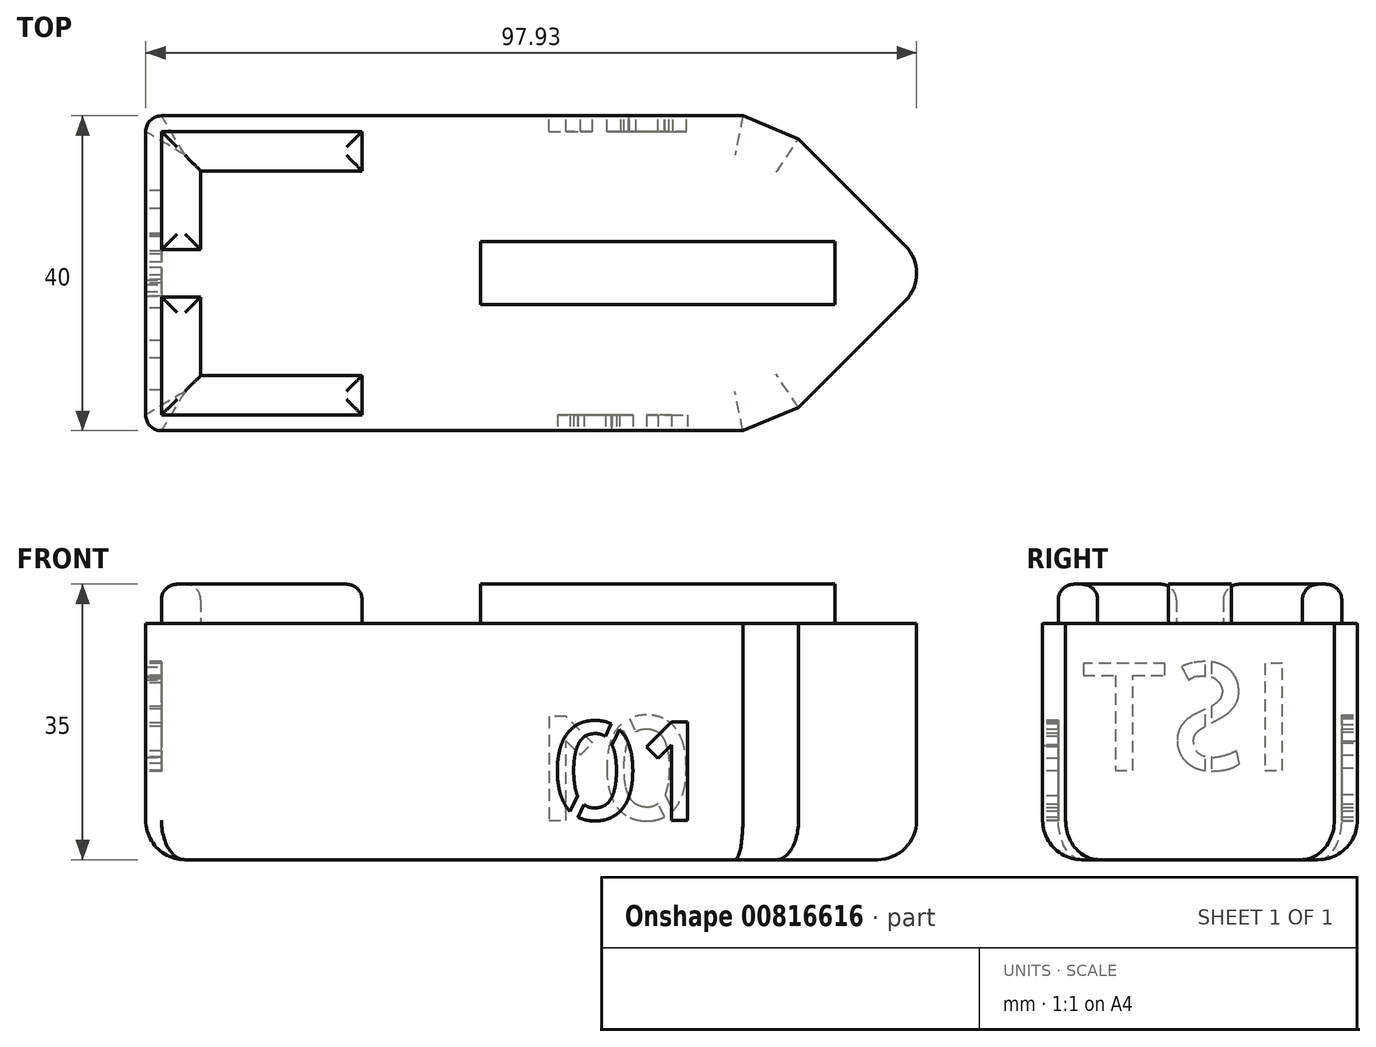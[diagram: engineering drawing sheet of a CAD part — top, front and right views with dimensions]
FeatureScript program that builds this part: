
annotation { "Feature Type Name" : "Feature", "Feature Type Description" : "" }
export const myFeature = defineFeature(function(context is Context, id is Id, definition is map)
    precondition{}
    {
        {
            var Q0;
            Q0=qCreatedBy(makeId("Top.planeOp"),FACE);
            var sketch = newSketch(context, id + "F0", { "sketchPlane" : qUnion([Q0])});
            skLineSegment(sketch, "E0.bottom", {"start": v(-50, 20) * mm, "end": v(50, 20) * mm});
            skLineSegment(sketch, "E0.top", {"start": v(-50, -20) * mm, "end": v(50, -20) * mm});
            skLineSegment(sketch, "E0.left", {"start": v(-50, 20) * mm, "end": v(-50, -20) * mm});
            skLineSegment(sketch, "E0.right", {"start": v(50, 20) * mm, "end": v(50, -20) * mm});
            skPoint(sketch, "E0.middle", {"position": v(0, 0) * mm});
            skSolve(sketch);
        }
        {
            var Q0;
            Q0 = qSketchRegion(id + "F0", true);
            extrude(context, id + "F1", {"entities" : qUnion([Q0]), "depth" : 30 * mm, "offsetDistance" : 25 * mm});
        }
        {
            var Q0;
            Q0=makeQuery(id+"F1.opExtrude","SWEPT_EDGE",EDGE,{"disambiguationData":[OSD([sQuery(id+"F0.wireOp",EDGE,"E0.top"),sQuery(id+"F0.wireOp",EDGE,"E0.right")])]});
            var Q1;
            Q1=makeQuery(id+"F1.opExtrude","SWEPT_EDGE",EDGE,{"disambiguationData":[OSD([sQuery(id+"F0.wireOp",EDGE,"E0.bottom"),sQuery(id+"F0.wireOp",EDGE,"E0.right")])]});
            chamfer(context, id + "F2", {"entities" : qUnion([Q0, Q1]), "width" : 20 * mm, "tangentPropagation" : true});
        }
        {
            var Q0;
            {var subQ0=sQuery(id+"F0.wireOp",EDGE,"E0.right");Q0=makeQuery(id+"F2.opChamfer","BLEND_EDGE",EDGE,{"blendedFrom":[makeQuery(id+"F1.opExtrude","SWEPT_EDGE",EDGE,{"disambiguationData":[OSD([sQuery(id+"F0.wireOp",EDGE,"E0.bottom"),subQ0])]}),makeQuery(id+"F1.opExtrude","SWEPT_EDGE",EDGE,{"disambiguationData":[OSD([sQuery(id+"F0.wireOp",EDGE,"E0.top"),subQ0])]})],"blendedInto":[]});}
            fillet(context, id + "F3", {"entities" : qUnion([Q0]), "radius" : 5 * mm, "tangentPropagation" : true, "allowEdgeOverflow" : false});
        }
        {
            var Q0;
            Q0=makeQuery(id+"F1.opExtrude","CAP_FACE",FACE,{"disambiguationData":[OSD([sQuery(id+"F0.wireOp",EDGE,"E0.bottom"),sQuery(id+"F0.wireOp",EDGE,"E0.top"),sQuery(id+"F0.wireOp",EDGE,"E0.left"),sQuery(id+"F0.wireOp",EDGE,"E0.right")])],"isStart":false});
            var sketch = newSketch(context, id + "F4", { "sketchPlane" : qUnion([Q0])});
            skPoint(sketch, "E1.middle", {"position": v(0, 0) * mm});
            skLineSegment(sketch, "E2", {"start": v(15.03, 0) * mm, "end": v(47.93, 0) * mm});
            skPoint(sketch, "E1.left.start.orphan", {"position": v(-22.5, 4) * mm});
            skPoint(sketch, "E1.top.start.orphan", {"position": v(-22.5, -4) * mm});
            skPoint(sketch, "E3.orphan", {"position": v(22.5, 4) * mm});
            skPoint(sketch, "E1.right.end.orphan", {"position": v(22.5, -4) * mm});
            skLineSegment(sketch, "E4.bottom", {"start": v(-7.47, 4) * mm, "end": v(37.53, 4) * mm});
            skLineSegment(sketch, "E4.top", {"start": v(-7.47, -4) * mm, "end": v(37.53, -4) * mm});
            skLineSegment(sketch, "E4.left", {"start": v(-7.47, 4) * mm, "end": v(-7.47, -4) * mm});
            skLineSegment(sketch, "E4.right", {"start": v(37.53, 4) * mm, "end": v(37.53, -4) * mm});
            skPoint(sketch, "E4.middle", {"position": v(15.03, 0) * mm});
            skSolve(sketch);
        }
        {
            var Q0;
            Q0=makeQuery(id+"F1.opExtrude","SWEPT_EDGE",EDGE,{"disambiguationData":[OSD([sQuery(id+"F0.wireOp",EDGE,"E0.top"),sQuery(id+"F0.wireOp",EDGE,"E0.left")])]});
            var Q1;
            Q1=makeQuery(id+"F1.opExtrude","SWEPT_EDGE",EDGE,{"disambiguationData":[OSD([sQuery(id+"F0.wireOp",EDGE,"E0.bottom"),sQuery(id+"F0.wireOp",EDGE,"E0.left")])]});
            fillet(context, id + "F5", {"entities" : qUnion([Q0, Q1]), "radius" : 2 * mm, "tangentPropagation" : true, "allowEdgeOverflow" : false});
        }
        {
            var Q0;
            Q0=makeQuery(id+"F1.opExtrude","CAP_FACE",FACE,{"disambiguationData":[OSD([sQuery(id+"F0.wireOp",EDGE,"E0.bottom"),sQuery(id+"F0.wireOp",EDGE,"E0.top"),sQuery(id+"F0.wireOp",EDGE,"E0.left"),sQuery(id+"F0.wireOp",EDGE,"E0.right")])],"isStart":false});
            var sketch = newSketch(context, id + "F6", { "sketchPlane" : qUnion([Q0])});
            skLineSegment(sketch, "E5.bottom", {"start": v(-48, 18) * mm, "end": v(-22.5, 18) * mm});
            skLineSegment(sketch, "E5.top", {"start": v(-48, 13) * mm, "end": v(-22.5, 13) * mm});
            skLineSegment(sketch, "E5.left", {"start": v(-48, 18) * mm, "end": v(-48, 13) * mm});
            skLineSegment(sketch, "E5.right", {"start": v(-22.5, 18) * mm, "end": v(-22.5, 13) * mm});
            skLineSegment(sketch, "E6.bottom", {"start": v(-48, -18) * mm, "end": v(-22.5, -18) * mm});
            skLineSegment(sketch, "E6.top", {"start": v(-48, -13) * mm, "end": v(-22.5, -13) * mm});
            skLineSegment(sketch, "E6.left", {"start": v(-48, -18) * mm, "end": v(-48, -13) * mm});
            skLineSegment(sketch, "E6.right", {"start": v(-22.5, -18) * mm, "end": v(-22.5, -13) * mm});
            skSolve(sketch);
        }
        {
            var Q0;
            Q0=makeQuery(id+"F6.imprint","IMPRINT",FACE,{"disambiguationData":[TD([[makeQuery(id+"F6.imprint","IMPRINT",EDGE,{"derivedFrom":sQuery(id+"F6.wireOp",EDGE,"E5.bottom")}),-1.0]])]});
            var Q1;
            Q1=makeQuery(id+"F6.imprint","IMPRINT",FACE,{"disambiguationData":[TD([[makeQuery(id+"F6.imprint","IMPRINT",EDGE,{"derivedFrom":sQuery(id+"F6.wireOp",EDGE,"E6.bottom")}),1.0]])]});
            extrude(context, id + "F7", {"entities" : qUnion([Q0, Q1]), "operationType" : NewBodyOperationType.ADD, "depth" : 5 * mm, "offsetDistance" : 25 * mm});
        }
        {
            var Q0;
            Q0=makeQuery(id+"F1.opExtrude","CAP_FACE",FACE,{"disambiguationData":[OSD([sQuery(id+"F0.wireOp",EDGE,"E0.bottom"),sQuery(id+"F0.wireOp",EDGE,"E0.top"),sQuery(id+"F0.wireOp",EDGE,"E0.left"),sQuery(id+"F0.wireOp",EDGE,"E0.right")])],"isStart":false});
            var sketch = newSketch(context, id + "F8", { "sketchPlane" : qUnion([Q0])});
            skLineSegment(sketch, "E7.bottom", {"start": v(-48, 13) * mm, "end": v(-43, 13) * mm});
            skLineSegment(sketch, "E7.top", {"start": v(-48, 3) * mm, "end": v(-43, 3) * mm});
            skLineSegment(sketch, "E7.left", {"start": v(-48, 13) * mm, "end": v(-48, 3) * mm});
            skLineSegment(sketch, "E7.right", {"start": v(-43, 13) * mm, "end": v(-43, 3) * mm});
            skLineSegment(sketch, "E8.bottom", {"start": v(-48, -13) * mm, "end": v(-43, -13) * mm});
            skLineSegment(sketch, "E8.top", {"start": v(-48, -3) * mm, "end": v(-43, -3) * mm});
            skLineSegment(sketch, "E8.left", {"start": v(-48, -13) * mm, "end": v(-48, -3) * mm});
            skLineSegment(sketch, "E8.right", {"start": v(-43, -13) * mm, "end": v(-43, -3) * mm});
            skSolve(sketch);
        }
        {
            var Q0;
            Q0=makeQuery(id+"F8.imprint","IMPRINT",FACE,{"disambiguationData":[TD([[makeQuery(id+"F8.imprint","IMPRINT",EDGE,{"derivedFrom":sQuery(id+"F8.wireOp",EDGE,"E7.bottom")}),-1.0]])]});
            var Q1;
            Q1=makeQuery(id+"F8.imprint","IMPRINT",FACE,{"disambiguationData":[TD([[makeQuery(id+"F8.imprint","IMPRINT",EDGE,{"derivedFrom":sQuery(id+"F8.wireOp",EDGE,"E8.bottom")}),1.0]])]});
            extrude(context, id + "F9", {"entities" : qUnion([Q0, Q1]), "operationType" : NewBodyOperationType.ADD, "depth" : 5 * mm, "offsetDistance" : 25 * mm});
        }
        {
            var Q0;
            {var subQ0=sQuery(id+"F0.wireOp",EDGE,"E0.top");Q0=makeQuery(id+"F2.opChamfer","BLEND_EDGE",EDGE,{"blendedFrom":[makeQuery(id+"F1.opExtrude","SWEPT_EDGE",EDGE,{"disambiguationData":[OSD([subQ0,sQuery(id+"F0.wireOp",EDGE,"E0.right")])]}),makeQuery(id+"F1.opExtrude","SWEPT_FACE",FACE,{"disambiguationData":[OSD([subQ0])]})],"blendedInto":[makeQuery(id+"F1.opExtrude","SWEPT_FACE",FACE,{"disambiguationData":[OSD([subQ0])]})]});}
            var Q1;
            {var subQ0=sQuery(id+"F0.wireOp",EDGE,"E0.bottom");Q1=makeQuery(id+"F2.opChamfer","BLEND_EDGE",EDGE,{"blendedFrom":[makeQuery(id+"F1.opExtrude","SWEPT_EDGE",EDGE,{"disambiguationData":[OSD([subQ0,sQuery(id+"F0.wireOp",EDGE,"E0.right")])]}),makeQuery(id+"F1.opExtrude","SWEPT_FACE",FACE,{"disambiguationData":[OSD([subQ0])]})],"blendedInto":[makeQuery(id+"F1.opExtrude","SWEPT_FACE",FACE,{"disambiguationData":[OSD([subQ0])]})]});}
            chamfer(context, id + "F10", {"entities" : qUnion([Q0, Q1]), "width" : 10 * mm, "tangentPropagation" : true});
        }
        {
            var Q0;
            Q0=makeQuery(id+"F1.opExtrude","CAP_FACE",FACE,{"disambiguationData":[OSD([sQuery(id+"F0.wireOp",EDGE,"E0.bottom"),sQuery(id+"F0.wireOp",EDGE,"E0.top"),sQuery(id+"F0.wireOp",EDGE,"E0.left"),sQuery(id+"F0.wireOp",EDGE,"E0.right")])],"isStart":true});
            fillet(context, id + "F11", {"entities" : qUnion([Q0]), "radius" : 5 * mm, "tangentPropagation" : true, "allowEdgeOverflow" : false});
        }
        {
            var Q0;
            Q0=makeQuery(id+"F1.opExtrude","SWEPT_FACE",FACE,{"disambiguationData":[OSD([sQuery(id+"F0.wireOp",EDGE,"E0.top")])]});
            var sketch = newSketch(context, id + "F12", { "sketchPlane" : qUnion([Q0])});
            skText(sketch, "E9", { "text": "01\n", "fontName": "AllertaStencil-Regular.ttf"});
            const initialGuessF12  = {"E9": [0.00104, 0.005, 1, 0, 0.0125]};
            skSetInitialGuess(sketch, initialGuessF12);
            skSolve(sketch);
        }
        {
            var Q0;
            Q0 = qSketchRegion(id + "F12", true);
            extrude(context, id + "F13", {"entities" : qUnion([Q0]), "operationType" : NewBodyOperationType.REMOVE, "oppositeDirection" : true, "depth" : 2 * mm, "offsetDistance" : 25 * mm});
        }
        {
            var Q0;
            Q0=makeQuery(id+"F1.opExtrude","SWEPT_FACE",FACE,{"disambiguationData":[OSD([sQuery(id+"F0.wireOp",EDGE,"E0.bottom")])]});
            var sketch = newSketch(context, id + "F14", { "sketchPlane" : qUnion([Q0])});
            skText(sketch, "E10", { "text": "01", "fontName": "AllertaStencil-Regular.ttf"});
            const initialGuessF14  = {"E10": [-0.02, 0.005, 1, 0, 0.01318]};
            skSetInitialGuess(sketch, initialGuessF14);
            skSolve(sketch);
        }
        {
            var Q0;
            Q0 = qSketchRegion(id + "F14", true);
            extrude(context, id + "F15", {"entities" : qUnion([Q0]), "operationType" : NewBodyOperationType.REMOVE, "oppositeDirection" : true, "depth" : 2 * mm, "offsetDistance" : 25 * mm});
        }
        {
            var Q0;
            Q0=makeQuery(id+"F9.boolean.opBoolean","MERGE",FACE,{"derivedFrom":[makeQuery(id+"F7.opExtrude","CAP_FACE",FACE,{"disambiguationData":[OSD([sQuery(id+"F6.wireOp",EDGE,"E5.bottom"),sQuery(id+"F6.wireOp",EDGE,"E5.top"),sQuery(id+"F6.wireOp",EDGE,"E5.left"),sQuery(id+"F6.wireOp",EDGE,"E5.right")])],"isStart":false}),makeQuery(id+"F9.opExtrude","CAP_FACE",FACE,{"disambiguationData":[OSD([sQuery(id+"F8.wireOp",EDGE,"E7.bottom"),sQuery(id+"F8.wireOp",EDGE,"E7.top"),sQuery(id+"F8.wireOp",EDGE,"E7.left"),sQuery(id+"F8.wireOp",EDGE,"E7.right")])],"isStart":false})]});
            var Q1;
            Q1=makeQuery(id+"F9.boolean.opBoolean","MERGE",FACE,{"derivedFrom":[makeQuery(id+"F7.opExtrude","CAP_FACE",FACE,{"disambiguationData":[OSD([sQuery(id+"F6.wireOp",EDGE,"E6.bottom"),sQuery(id+"F6.wireOp",EDGE,"E6.top"),sQuery(id+"F6.wireOp",EDGE,"E6.left"),sQuery(id+"F6.wireOp",EDGE,"E6.right")])],"isStart":false}),makeQuery(id+"F9.opExtrude","CAP_FACE",FACE,{"disambiguationData":[OSD([sQuery(id+"F8.wireOp",EDGE,"E8.bottom"),sQuery(id+"F8.wireOp",EDGE,"E8.top"),sQuery(id+"F8.wireOp",EDGE,"E8.left"),sQuery(id+"F8.wireOp",EDGE,"E8.right")])],"isStart":false})]});
            fillet(context, id + "F16", {"entities" : qUnion([Q0, Q1]), "radius" : 2 * mm, "tangentPropagation" : true, "allowEdgeOverflow" : false});
        }
        {
            var Q0;
            Q0=makeQuery(id+"F1.opExtrude","SWEPT_FACE",FACE,{"disambiguationData":[OSD([sQuery(id+"F0.wireOp",EDGE,"E0.left")])]});
            var sketch = newSketch(context, id + "F17", { "sketchPlane" : qUnion([Q0])});
            skText(sketch, "E11", { "text": "IST", "fontName": "AllertaStencil-Regular.ttf"});
            const initialGuessF17  = {"E11": [-0.01222, 0.01132, 1, 0, 0.01364]};
            skSetInitialGuess(sketch, initialGuessF17);
            skSolve(sketch);
        }
        {
            var Q0;
            Q0 = qSketchRegion(id + "F17", true);
            extrude(context, id + "F18", {"entities" : qUnion([Q0]), "operationType" : NewBodyOperationType.REMOVE, "oppositeDirection" : true, "depth" : 2 * mm, "offsetDistance" : 25 * mm});
        }
        {
            var Q0;
            Q0 = qSketchRegion(id + "F4", true);
            extrude(context, id + "F19", {"entities" : qUnion([Q0]), "operationType" : NewBodyOperationType.ADD, "depth" : 5 * mm, "offsetDistance" : 25 * mm});
        }
    });
